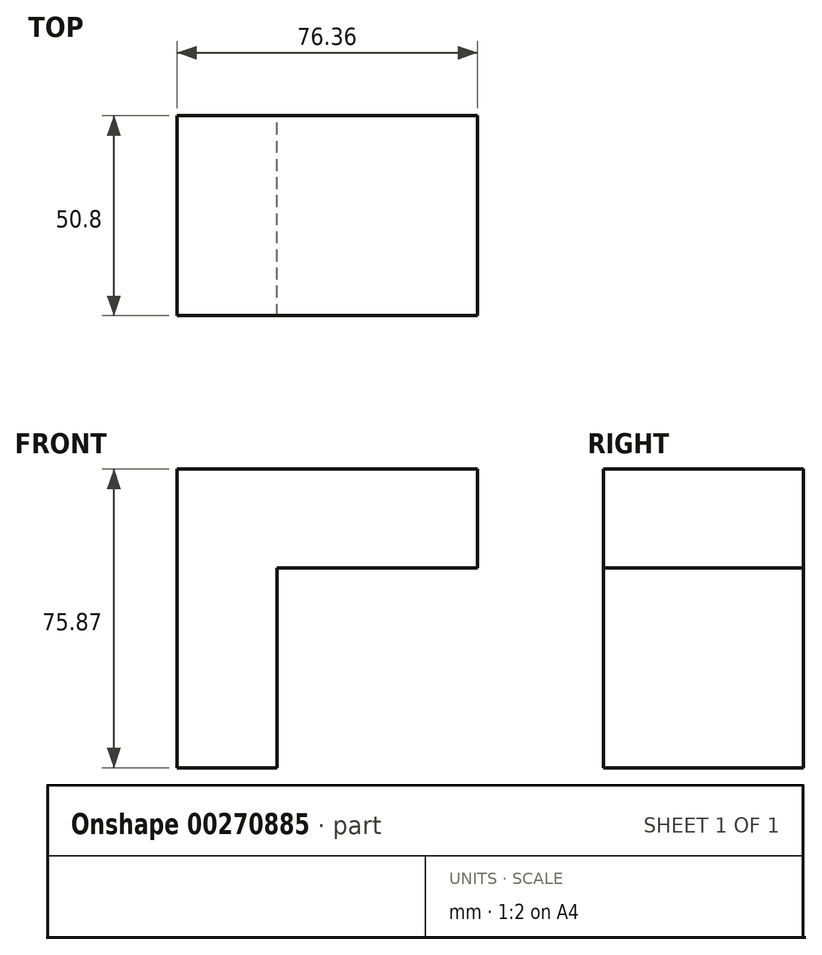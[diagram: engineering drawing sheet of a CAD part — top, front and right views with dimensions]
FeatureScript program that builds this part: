
annotation { "Feature Type Name" : "Feature", "Feature Type Description" : "" }
export const myFeature = defineFeature(function(context is Context, id is Id, definition is map)
    precondition{}
    {
        {
            var Q0;
            Q0=qCreatedBy(makeId("Front.planeOp"),FACE);
            var sketch = newSketch(context, id + "F0", { "sketchPlane" : qUnion([Q0])});
            skLineSegment(sketch, "E0", {"start": v(-76.36, 0) * mm, "end": v(-76.36, 75.87) * mm});
            skLineSegment(sketch, "E1", {"start": v(-76.36, 75.87) * mm, "end": v(0, 75.87) * mm});
            skLineSegment(sketch, "E2", {"start": v(-76.36, 0) * mm, "end": v(-50.96, 0) * mm});
            skLineSegment(sketch, "E3", {"start": v(-50.96, 0) * mm, "end": v(-50.96, 50.8) * mm});
            skLineSegment(sketch, "E4", {"start": v(-50.96, 50.8) * mm, "end": v(0, 50.8) * mm});
            skLineSegment(sketch, "E5", {"start": v(0, 75.87) * mm, "end": v(0, 48.24) * mm});
            skSolve(sketch);
        }
        {
            var Q0;
            Q0 = qSketchRegion(id + "F0", true);
            extrude(context, id + "F1", {"entities" : qUnion([Q0]), "depth" : 50.8 * mm});
        }
    });
